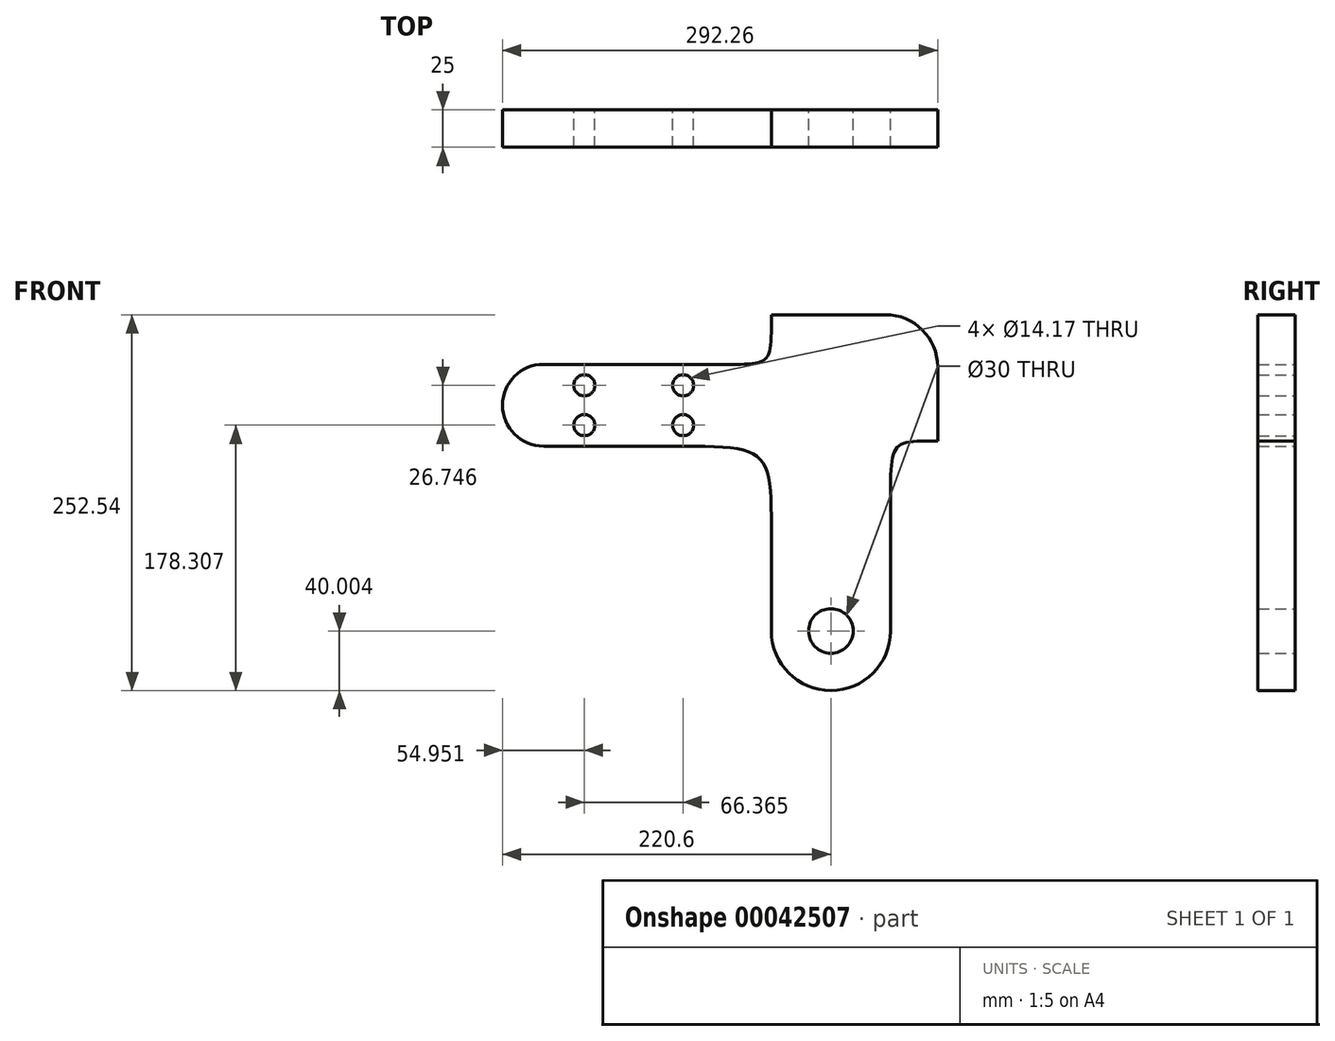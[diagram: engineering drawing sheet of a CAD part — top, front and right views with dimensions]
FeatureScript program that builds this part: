
annotation { "Feature Type Name" : "Feature", "Feature Type Description" : "" }
export const myFeature = defineFeature(function(context is Context, id is Id, definition is map)
    precondition{}
    {
        {
            var Q0;
            Q0=qCreatedBy(makeId("Front.planeOp"),FACE);
            var sketch = newSketch(context, id + "F0", { "sketchPlane" : qUnion([Q0])});
            skLineSegment(sketch, "E0.bottom", {"start": v(-31.84, 27.5) * mm, "end": v(-153.1, 27.5) * mm});
            skLineSegment(sketch, "E0.top", {"start": v(-67.9, -27.5) * mm, "end": v(-153.1, -27.5) * mm});
            skLineSegment(sketch, "E0.left", {"start": v(80, -23.65) * mm, "end": v(80, -23.97) * mm});
            skLineSegment(sketch, "E1.top", {"start": v(80, -151.68) * mm, "end": v(80, -151.68) * mm});
            skLineSegment(sketch, "E1.right", {"start": v(0, -89.59) * mm, "end": v(0, -151.68) * mm});
            skArc(sketch, "E2", {"start": v(0, -151.68) * mm, "mid": v(40, -191.68) * mm, "end": v(80, -151.68) * mm});
            skArc(sketch, "E3", {"start": v(-153.1, 27.5) * mm, "mid": v(-180.6, 0) * mm, "end": v(-153.1, -27.5) * mm});
            skLineSegment(sketch, "E4.filletArc", {"start": v(0, -27.5) * mm, "end": v(0, -27.5) * mm});
            skFitSpline(sketch, "E5", {"points": [v(-67.9, -27.5) * mm, v(0, -89.59) * mm], "startDerivative": vector(203.7, 0) * mm, "endDerivative": vector(0, -186.26) * mm});
            skFitSpline(sketch, "E6", {"points": [v(0, 60.86) * mm, v(-31.84, 27.5) * mm], "startDerivative": vector(0, -103.64) * mm, "endDerivative": vector(-95.5, 0) * mm});
            skFitSpline(sketch, "E7", {"points": [v(111.66, -24.14) * mm, v(80, -64.58) * mm], "startDerivative": vector(-94.98, 1.46) * mm, "endDerivative": vector(0, -121.82) * mm});
            skLineSegment(sketch, "E8.trimOffspring", {"start": v(80, -64.58) * mm, "end": v(80, -151.68) * mm});
            skLineSegment(sketch, "E9.trimOffspring", {"start": v(0, -151.68) * mm, "end": v(0, -151.68) * mm});
            skCircle(sketch, "E10", {"center": v(40, -151.68) * mm, "radius": 15 * mm});
            skPoint(sketch, "E11.startSnap0", {"position": v(-92.47, 27.5) * mm});
            skCircle(sketch, "E12", {"center": v(-125.65, 13.37) * mm, "radius": 7.09 * mm});
            skCircle(sketch, "E13.MirrorC", {"center": v(-125.65, -13.37) * mm, "radius": 7.09 * mm});
            skCircle(sketch, "E14.MirrorC", {"center": v(-59.28, -13.37) * mm, "radius": 7.09 * mm});
            skCircle(sketch, "E15.MirrorC", {"center": v(-59.28, 13.37) * mm, "radius": 7.09 * mm});
            skLineSegment(sketch, "E16", {"start": v(0, 60.86) * mm, "end": v(111.66, 60.86) * mm});
            skLineSegment(sketch, "E17", {"start": v(111.66, 60.86) * mm, "end": v(111.66, -24.14) * mm});
            skSolve(sketch);
        }
        {
            var Q0;
            {var subQ0=sQuery(id+"F0.wireOp",EDGE,"E0.bottom");Q0=makeQuery(id+"F0.imprint","IMPRINT",FACE,{"disambiguationData":[TD([[makeQuery(id+"F0.imprint","IMPRINT",EDGE,{"derivedFrom":subQ0}),1.0]])]});}
            extrude(context, id + "F1", {"entities" : qUnion([Q0]), "depth" : 25 * mm});
        }
        {
            var Q0;
            Q0=makeQuery(id+"F1.opExtrude","SWEPT_EDGE",EDGE,{"disambiguationData":[OSD([sQuery(id+"F0.wireOp",EDGE,"E16"),sQuery(id+"F0.wireOp",EDGE,"E17")])]});
            fillet(context, id + "F2", {"entities" : qUnion([Q0]), "radius" : 35 * mm, "tangentPropagation" : true, "allowEdgeOverflow" : false});
        }
    });
